# Revit family: Layout-Teknion-Zones_Coffee_Lounge_Zone_Four-R2022
name_source: partatom
category: Electrical Fixtures
units: mm (PartAtom-declared; Revit-internal decimal feet)

## family parameters
Always vertical = Yes
Cut with Voids When Loaded = No
Maintain Annotation Orientation = No
OmniClass Number = 23.40.70.14.64.21
OmniClass Title = Systems Furniture
Part Type = Normal
Room Calculation Point = No
Round Connector Dimension = Use Diameter
Shared = Yes
Work Plane-Based = No

## types (1)
- Coffee Lounge Four 01
    Assembly Code = E2020200
    Default Elevation = 0' - 0"
    Depth = 0' - 0"
    Description = Coffee Lounge Zone Four - 01
    Height = 2' - 5"
    Length = 0' - 0"
    Manufacturer = Teknion
    Manufacturer Fax = 416.661.4586
    Model = 5'-10" x 9'-5" Overall Cluster
    Product Line = Zones
    Product Page URL = http://teknionplanningtool.com
    Series = Zones
    Sustainability Data = http://www.teknion.com
    URL = www.teknion.com
    Unit Weight URL = http://www.teknion.com
    Warranty = http://www.teknion.com
    Width = 0' - 0"

## geometry (parser evidence)
native form markers: Blend x8, Sweep x26
no freeform markers — native parametric forms only
